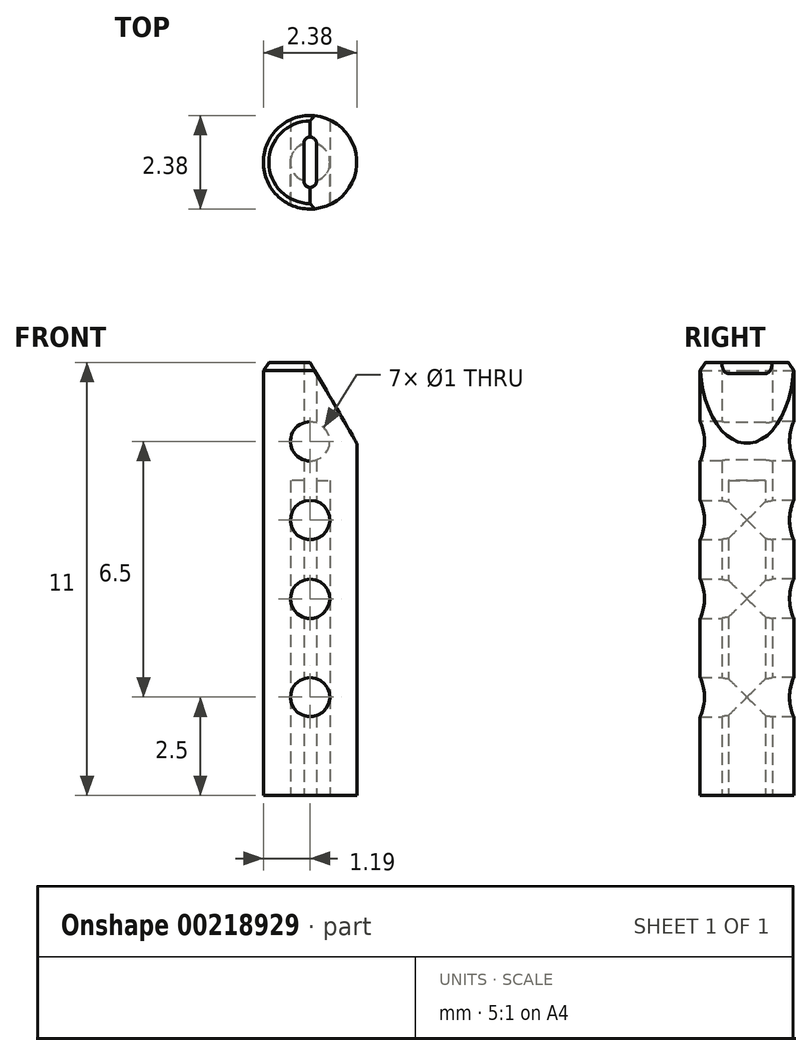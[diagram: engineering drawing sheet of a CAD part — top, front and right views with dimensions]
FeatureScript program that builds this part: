
annotation { "Feature Type Name" : "Feature", "Feature Type Description" : "" }
export const myFeature = defineFeature(function(context is Context, id is Id, definition is map)
    precondition{}
    {
        {
            var Q0;
            Q0=qCreatedBy(makeId("Right.planeOp"),FACE);
            var sketch = newSketch(context, id + "F0", { "sketchPlane" : qUnion([Q0])});
            skLineSegment(sketch, "E0", {"start": v(0, 0) * mm, "end": v(0, 11) * mm});
            skLineSegment(sketch, "E1", {"start": v(0, 11) * mm, "end": v(-1.05, 11) * mm});
            skLineSegment(sketch, "E2", {"start": v(-1.2, 10.8) * mm, "end": v(-1.19, 0) * mm});
            skLineSegment(sketch, "E3", {"start": v(-1.19, 0) * mm, "end": v(0, 0) * mm});
            skLineSegment(sketch, "E4", {"start": v(-1.05, 11) * mm, "end": v(-1.2, 10.8) * mm});
            skSolve(sketch);
        }
        {
            var Q0;
            Q0=makeQuery(id+"F0.imprint","IMPRINT",FACE,{"disambiguationData":[TD([[makeQuery(id+"F0.imprint","IMPRINT",EDGE,{"derivedFrom":sQuery(id+"F0.wireOp",EDGE,"E0")}),1.0]])]});
            var Q1;
            Q1=sQuery(id+"F0.wireOp",EDGE,"E0");
            revolve(context, id + "F1", {"entities" : qUnion([Q0]), "axis" : qUnion([Q1]), "revolveType" : RevolveType.FULL});
        }
        {
            var Q0;
            Q0=makeQuery(id+"F1.opRevolve","SWEPT_FACE",FACE,{"disambiguationData":[OSD([sQuery(id+"F0.wireOp",EDGE,"E3")])]});
            var sketch = newSketch(context, id + "F2", { "sketchPlane" : qUnion([Q0])});
            skCircle(sketch, "E5", {"center": v(0, 0) * mm, "radius": 0.5 * mm});
            skSolve(sketch);
        }
        {
            var Q0;
            Q0=qSketchRegion(id+"F2",true);
            extrude(context, id + "F3", {"entities" : qUnion([Q0]), "operationType" : NewBodyOperationType.REMOVE, "oppositeDirection" : true, "depth" : 8 * mm});
        }
        {
            var Q0;
            Q0=qCreatedBy(makeId("Front.planeOp"),FACE);
            var sketch = newSketch(context, id + "F4", { "sketchPlane" : qUnion([Q0])});
            skCircle(sketch, "E6", {"center": v(0, 20.84) * mm, "radius": 0.71 * mm});
            skCircle(sketch, "E7", {"center": v(0, 9) * mm, "radius": 0.5 * mm});
            skCircle(sketch, "E8", {"center": v(0, 7) * mm, "radius": 0.5 * mm});
            skCircle(sketch, "E9", {"center": v(0, 5) * mm, "radius": 0.5 * mm});
            skCircle(sketch, "E10", {"center": v(0, 2.5) * mm, "radius": 0.5 * mm});
            skCircle(sketch, "E11", {"center": v(0, 12) * mm, "radius": 0.5 * mm});
            skSolve(sketch);
        }
        {
            var Q0;
            Q0=qSketchRegion(id+"F4",true);
            extrude(context, id + "F5", {"entities" : qUnion([Q0]), "operationType" : NewBodyOperationType.REMOVE, "oppositeDirection" : true, "depth" : 25 * mm});
        }
        {
            var Q0;
            Q0=qSketchRegion(id+"F4",true);
            extrude(context, id + "F6", {"entities" : qUnion([Q0]), "operationType" : NewBodyOperationType.REMOVE, "depth" : 25 * mm});
        }
        {
            var Q0;
            Q0=qCreatedBy(makeId("Front.planeOp"),FACE);
            var sketch = newSketch(context, id + "F7", { "sketchPlane" : qUnion([Q0])});
            skLineSegment(sketch, "E12", {"start": v(0, 11) * mm, "end": v(1.58, 11) * mm});
            skLineSegment(sketch, "E13", {"start": v(1.58, 11) * mm, "end": v(1.58, 8.26) * mm});
            skLineSegment(sketch, "E14", {"start": v(1.58, 8.26) * mm, "end": v(0, 11) * mm});
            skSolve(sketch);
        }
        {
            var Q0;
            Q0=qSketchRegion(id+"F7",true);
            extrude(context, id + "F8", {"entities" : qUnion([Q0]), "operationType" : NewBodyOperationType.REMOVE, "oppositeDirection" : true, "depth" : 5 * mm});
        }
        {
            var Q0;
            Q0=qSketchRegion(id+"F7",true);
            extrude(context, id + "F9", {"entities" : qUnion([Q0]), "operationType" : NewBodyOperationType.REMOVE, "depth" : 25 * mm});
        }
        {
            var Q0;
            Q0=qCreatedBy(makeId("Top.planeOp"),FACE);
            var sketch = newSketch(context, id + "F10", { "sketchPlane" : qUnion([Q0])});
            skLineSegment(sketch, "E15", {"start": v(-0.16, 0.48) * mm, "end": v(-0.16, -0.48) * mm});
            skLineSegment(sketch, "E16", {"start": v(0.16, 0.48) * mm, "end": v(0.16, -0.48) * mm});
            skArc(sketch, "E17", {"start": v(-0.16, 0.48) * mm, "mid": v(0, 0.64) * mm, "end": v(0.16, 0.48) * mm});
            skArc(sketch, "E18", {"start": v(-0.16, -0.48) * mm, "mid": v(0, -0.64) * mm, "end": v(0.16, -0.48) * mm});
            skSolve(sketch);
        }
        {
            var Q0;
            Q0 = qSketchRegion(id + "F10", true);
            extrude(context, id + "F11", {"entities" : qUnion([Q0]), "operationType" : NewBodyOperationType.REMOVE, "depth" : 25 * mm});
        }
    });
